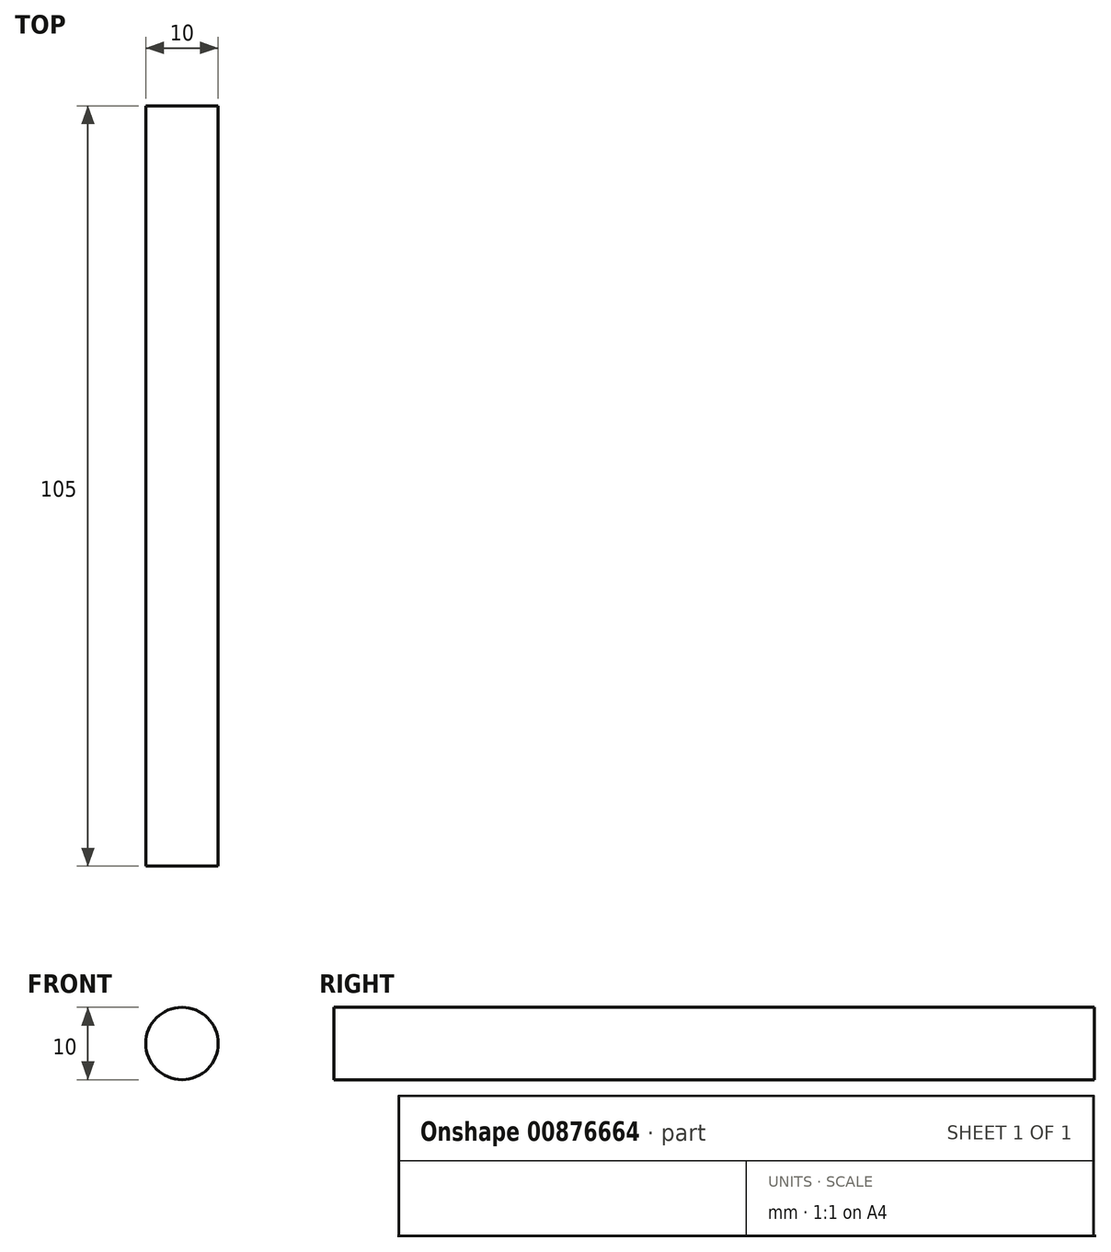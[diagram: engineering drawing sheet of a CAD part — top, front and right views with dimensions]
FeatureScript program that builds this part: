
annotation { "Feature Type Name" : "Feature", "Feature Type Description" : "" }
export const myFeature = defineFeature(function(context is Context, id is Id, definition is map)
    precondition{}
    {
        {
            var Q0;
            Q0=qCreatedBy(makeId("Front.planeOp"),FACE);
            var sketch = newSketch(context, id + "F0", { "sketchPlane" : qUnion([Q0])});
            skCircle(sketch, "E0", {"center": v(0, 0) * mm, "radius": 5 * mm});
            skSolve(sketch);
        }
        {
            var Q0;
            Q0=makeQuery(id+"F0.imprint","IMPRINT",FACE,{"disambiguationData":[TD([[makeQuery(id+"F0.imprint","IMPRINT",EDGE,{"derivedFrom":sQuery(id+"F0.wireOp",EDGE,"E0")}),-1.0]])]});
            var Q1;
            Q1=makeQuery(id+"F0.imprint","IMPRINT",FACE,{"disambiguationData":[TD([[makeQuery(id+"F0.imprint","IMPRINT",EDGE,{"derivedFrom":sQuery(id+"F0.wireOp",EDGE,"E0")}),1.0]])]});
            extrude(context, id + "F1", {"entities" : qUnion([Q0, Q1]), "depth" : 105 * mm, "offsetDistance" : 25 * mm});
        }
    });
